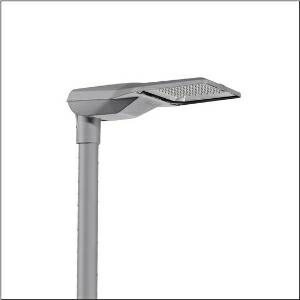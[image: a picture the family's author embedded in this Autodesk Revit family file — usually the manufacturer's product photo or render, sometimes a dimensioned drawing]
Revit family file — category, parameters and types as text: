
# Revit family: streetlight_sl_21_iq_midi___st1_0a_5xe3d31d08nb_3762
name_source: partatom
category: Lighting Fixtures
units: mm (PartAtom-declared; Revit-internal decimal feet)

## family parameters
Cut with Voids When Loaded = No
Host = Face
Light Source = No
Part Type = Normal
Room Calculation Point = No
Round Connector Dimension = Use Diameter
Shared = No

## types (1)
- --- (1 x LED, 23230 lm, 155.5 W, 3000K)
    Apparent Load = 155 VA
    CIE Flux Codes = 40 73 97 100 100
    Color Rendering = 70
    Color Temperature = 3000K
    Default Elevation = 1800 mm
    Description = Streetlight SL 21 iQ midi, mast luminaire, primary light control with lens, of PMMA, primary optical cover: cover, of toughened safety glass, transparent, light distribution: ST1.0a, light emission: direct distribution, primary light characteristic: asymmetric, installation type: post-top, side-entry, LED, High Power LED, rated luminous flux: 23.230lm, luminous efficacy: 149lm/W, light colour: 730, colour temperature: 3000K, control gear: iQ-Comfort, control: Auto-Match, Temp-Guard, Lumen-Switch, Night-Set, Smart-Wire, Light-Fading, Desk-Remote (wireless, voltage-free reading and setting of iQ features in the workshop via application-optimized NFC function/RFID function), optimised constant luminous flux control (CLO 2.0), pre-setting: linear dimming characteristic, mains connection: 230..240V, AC, 50/60Hz, start of lifetime: 156W, end of service life: 162W, reduction: 69W, luminaire housing, of diecast aluminium, powder-coated, SITECO metallic grey (DB 702S), corrosivity category C5 high according to DIN EN ISO 12944, please order mast flange separately, inclination adjustable: 0°, 5°, 10°, 15°, sealing non-destructively replaceable, multi-level sealing system, length: 644mm, width: 335mm, height: 110mm, mast flange for spigot size: 42mm (side-entry): 5XC10008XM4, 60/48mm (side-entry/post-top): 5XC10108XM2, 76/60mm (side-entry/post-top): 5XC10108XM1, mounting height: 4..8m, protection rating (complete): IP66, insulation class (complete): insulation class II (safety insulation), certification: CE, ENEC, ENEC+, VDE, impact resistance: IK10, permissible operating ambient temperature for outdoor applications: -40..+50°C, standard-compliant lighting for roads and squares, packaging unit: 1 piece

Light Distribution: ST1.0a
    Height = 111 mm
    Lamp = 1 x LED
    Lamp Light Flux = 23230 lm
    Lamp Power = 155.5 W
    Lamp count = 1
    Length = 644 mm
    Luminous efficacy = 149 lm/W
    Manufacturer = Siteco
    ModVariant = No
    Model = 5XE3D31D08NB
    Number of Poles = 1
    OnlyDefault = Yes
    Power Factor = 1
    Product Name = Streetlight SL 21 iQ midi | ST1.0a
    Product group = mast luminaire | pylon top
    ProductGroupID = 6100
    Protection Class = Protection class II
    Protection Degree = IP 66
    RLX_Detail_Level = 1
    RLX_Emergency_Light_Flux = 0 lm
    RLX_Emergency_Type = 0
    RLX_Emergency_Type_DB = No
    RlxData = <blob elided: 27241 chars, md5=df7ab811>
    Socket = socket
    Standby Power = 0 W
    System Light Flux = 23230 lm
    System Power = 155 W
    Type Comments = factory setting: luminous flux: 100 % | dim-lin: 254 | 823 mA
    Type Image = l_1004298.jpg
    URL = http://relux.com
    VarID = @adj_170367
    Voltage = 0 V
    Weight = 0.00 kg
    Width = 336 mm

## geometry (parser evidence)
native form markers: Blend x4, Sweep x10
no freeform markers — native parametric forms only
